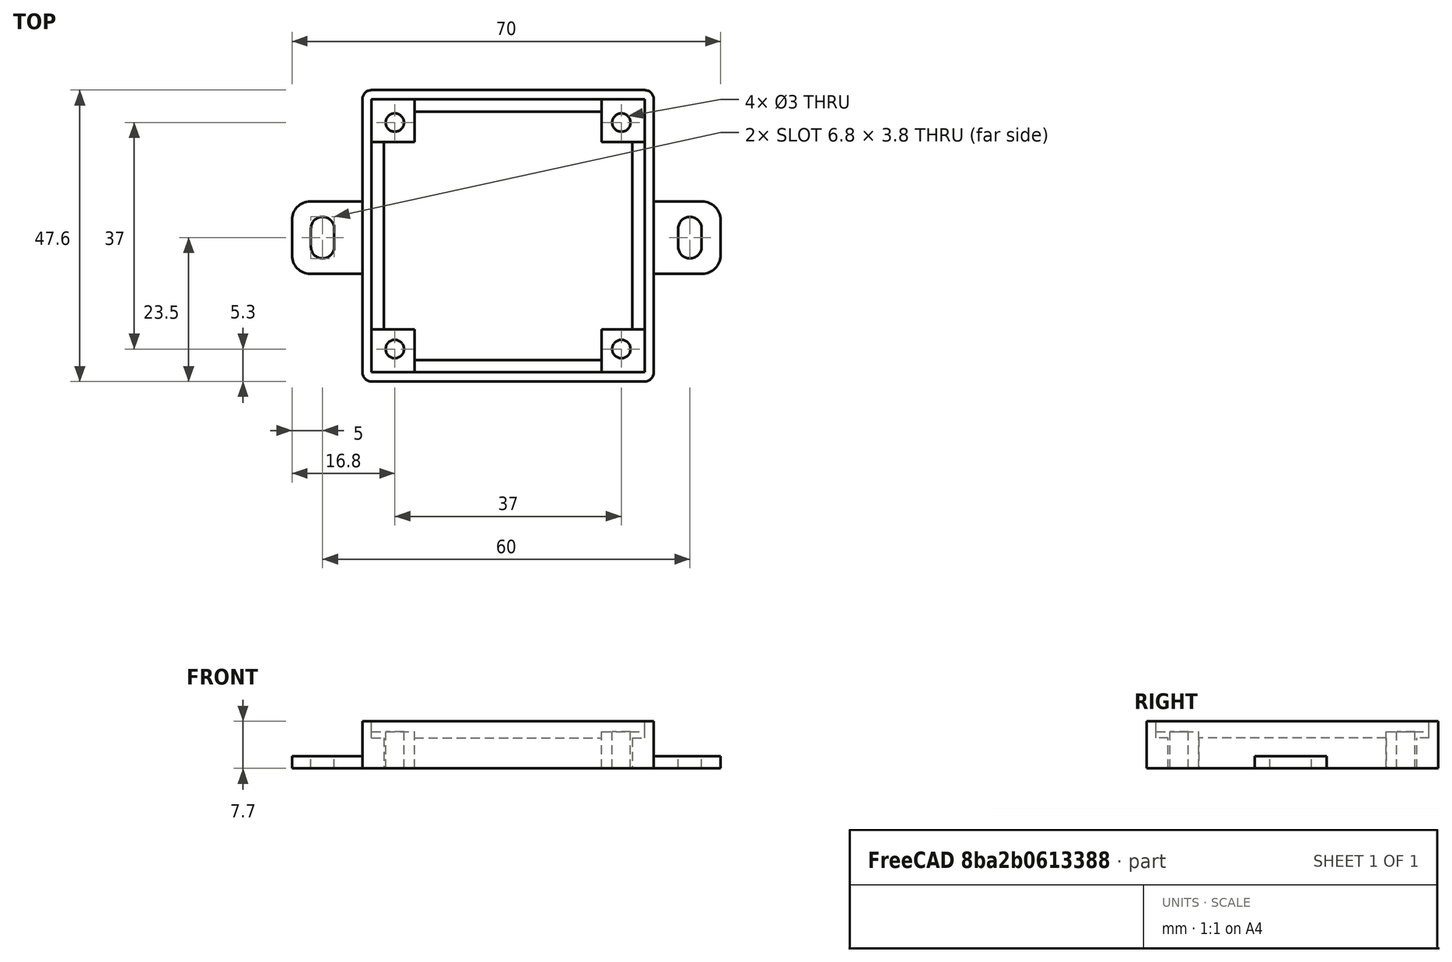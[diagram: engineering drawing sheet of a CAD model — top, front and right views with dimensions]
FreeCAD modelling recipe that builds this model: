
FCSTD DOCUMENT  (FreeCAD 0.19R23578 (Git))
Label: motor-driver-l298n
License: All rights reserved
LicenseURL: http://en.wikipedia.org/wiki/All_rights_reserved
objects: Part::Box×4, Part::MultiFuse×3, Part::FeaturePython×2, Part::Cut×2, Spreadsheet::Sheet×1, Part::Cylinder×1, Part::Fillet×1, Part::Feature×1, App::Part×1
note: 14 computed .brp shape members not serialized (recipe doc carries the construction recipe); baked Part::Feature solids carry a one-line shape summary decoded from their .brp

FEATURE [Spreadsheet::Sheet] Spreadsheet  label="p"
  cells = A1=hole_x_dist; B1(hole_x_dist)=37; A2=hole_y_dist; B2(hole_y_dist)=37; A3=pcb_under; B3(pcb_under)=3; A4=pcb_x; B4(pcb_x)=44.6; A5=pcb_y; B5(pcb_y)=44.6; A6=hole_stand_x; B6(hole_stand_x)=7; A7=hole_stand_y; B7(hole_stand_y)=7; A8=hole_r; B8(hole_r)=1.5; A9=box_wall; B9(box_wall)=1.5; A10=under_layer; B10(under_layer)=3; A11=pcb_height; B11(pcb_height)=1.7; A12=under_pcb_border; B12(under_pcb_border)=2
FEATURE [Part::Box] Box  label="bottom cube"
  AttacherType = Attacher::AttachEngine3D
  Height = 7.7
  Length = 47.6
  Width = 47.6
  expr: Height = <<p>>.pcb_under + <<p>>.pcb_height + <<p>>.under_layer
  expr: Length = <<p>>.pcb_x + <<p>>.box_wall * 2
  expr: Width = <<p>>.pcb_y + <<p>>.box_wall * 2
FEATURE [Part::Box] Box001  label="bottom extraction"
  AttacherType = Attacher::AttachEngine3D
  Height = 10
  Length = 40.6
  Placement = pos=(3.5,3.5,0) rot=(0,0,1;0rad)
  Width = 40.6
  expr: Width = <<p>>.pcb_y - <<p>>.under_pcb_border * 2
  expr: Length = <<p>>.pcb_x - <<p>>.under_pcb_border * 2
  expr: .Placement.Base.x = <<p>>.under_pcb_border + <<p>>.box_wall
  expr: .Placement.Base.y = <<p>>.under_pcb_border + <<p>>.box_wall
FEATURE [Part::Box] Box002  label="pcb extraction"
  AttacherType = Attacher::AttachEngine3D
  Height = 10
  Length = 44.6
  Placement = pos=(1.5,1.5,5) rot=(0,0,1;0rad)
  Width = 44.6
  expr: Width = <<p>>.pcb_y
  expr: Length = <<p>>.pcb_x
  expr: .Placement.Base.x = <<p>>.box_wall
  expr: .Placement.Base.y = <<p>>.box_wall
  expr: .Placement.Base.z = <<p>>.under_pcb_border + <<p>>.under_layer
FEATURE [Part::MultiFuse] Fusion  label="bottom extraction001"
  Shapes = -> [Box001,Box002]
FEATURE [Part::Box] Box003  label="hole stand cube"
  AttacherType = Attacher::AttachEngine3D
  Height = 6
  Length = 7
  Placement = pos=(1.5,1.5,0) rot=(0,0,1;0rad)
  Width = 7
  expr: Length = <<p>>.hole_stand_x
  expr: Width = <<p>>.hole_stand_y
  expr: Height = <<p>>.pcb_under + <<p>>.under_layer
  expr: .Placement.Base.x = <<p>>.box_wall
  expr: .Placement.Base.y = <<p>>.box_wall
FEATURE [Part::FeaturePython] Array  label="hole stand array"  # Draft array (typed FeaturePython)
  Angle = 360
  ArrayType = 0
  Axis = (0,0,1)
  Base = -> Box003
  Center = (0,0,0)
  Fuse = false
  IntervalAxis = (0,0,0)
  IntervalX = (37.6,0,0)
  IntervalY = (0,37.6,0)
  IntervalZ = (0,0,1)
  NumberPolar = 1
  NumberX = 2
  NumberY = 2
  NumberZ = 1
  expr: .IntervalX.x = <<p>>.pcb_x - <<p>>.hole_stand_x
  expr: .IntervalY.y = <<p>>.pcb_y - <<p>>.hole_stand_y
FEATURE [Part::Cylinder] Cylinder  label="pcb hole"
  Angle = 360
  AttacherType = Attacher::AttachEngine3D
  Height = 10
  Placement = pos=(5.3,5.3,0) rot=(0,0,1;0rad)
  Radius = 1.5
  expr: Radius = <<p>>.hole_r
  expr: .Placement.Base.x = (<<p>>.box_wall * 2 + <<p>>.pcb_x - <<p>>.hole_x_dist) / 2
  expr: .Placement.Base.y = (<<p>>.box_wall * 2 + <<p>>.pcb_y - <<p>>.hole_y_dist) / 2
FEATURE [Part::FeaturePython] Array001  label="hole array"  # Draft array (typed FeaturePython)
  Angle = 360
  ArrayType = 0
  Axis = (0,0,1)
  Base = -> Cylinder
  Center = (0,0,0)
  Fuse = false
  IntervalAxis = (0,0,0)
  IntervalX = (37,0,0)
  IntervalY = (0,37,0)
  IntervalZ = (0,0,1)
  NumberPolar = 1
  NumberX = 2
  NumberY = 2
  NumberZ = 1
  expr: .IntervalX.x = <<p>>.hole_x_dist
  expr: .IntervalY.y = <<p>>.hole_y_dist
FEATURE [Part::Fillet] Fillet001  label="bottom cube fillet"
  Base = -> Box
  Edges = 4 edges r=1.5: [Edge1,Edge3,Edge5,Edge7]
FEATURE [Part::Feature] Cut003001  label="attach plane x dir001"
  Placement = pos=(-11.5,17.6,0) rot=(0,0,1;0rad)
  shape: bbox 70 x 11.8 x 2 mm, 18 faces (baked)
FEATURE [Part::MultiFuse] Fusion002  label="bottom fusion"
  Shapes = -> [Fillet001,Cut003001]
FEATURE [Part::Cut] Cut  label="pcb box cut"
  Base = -> Fusion002
  Tool = -> Fusion
FEATURE [Part::MultiFuse] Fusion001  label="frame fusion"
  Shapes = -> [Array,Cut]
FEATURE [Part::Cut] Cut001  label="frame fusion with holes"
  Base = -> Fusion001
  Tool = -> Array001
FEATURE [App::Part] Part  label="pcb with 4 holes part"
  Group = -> [Fusion,Fusion002,Box002,Box003,Box001,Array001,Box,Cut,Array,Cylinder,Fusion001,Cut001]
  Origin = -> Origin
